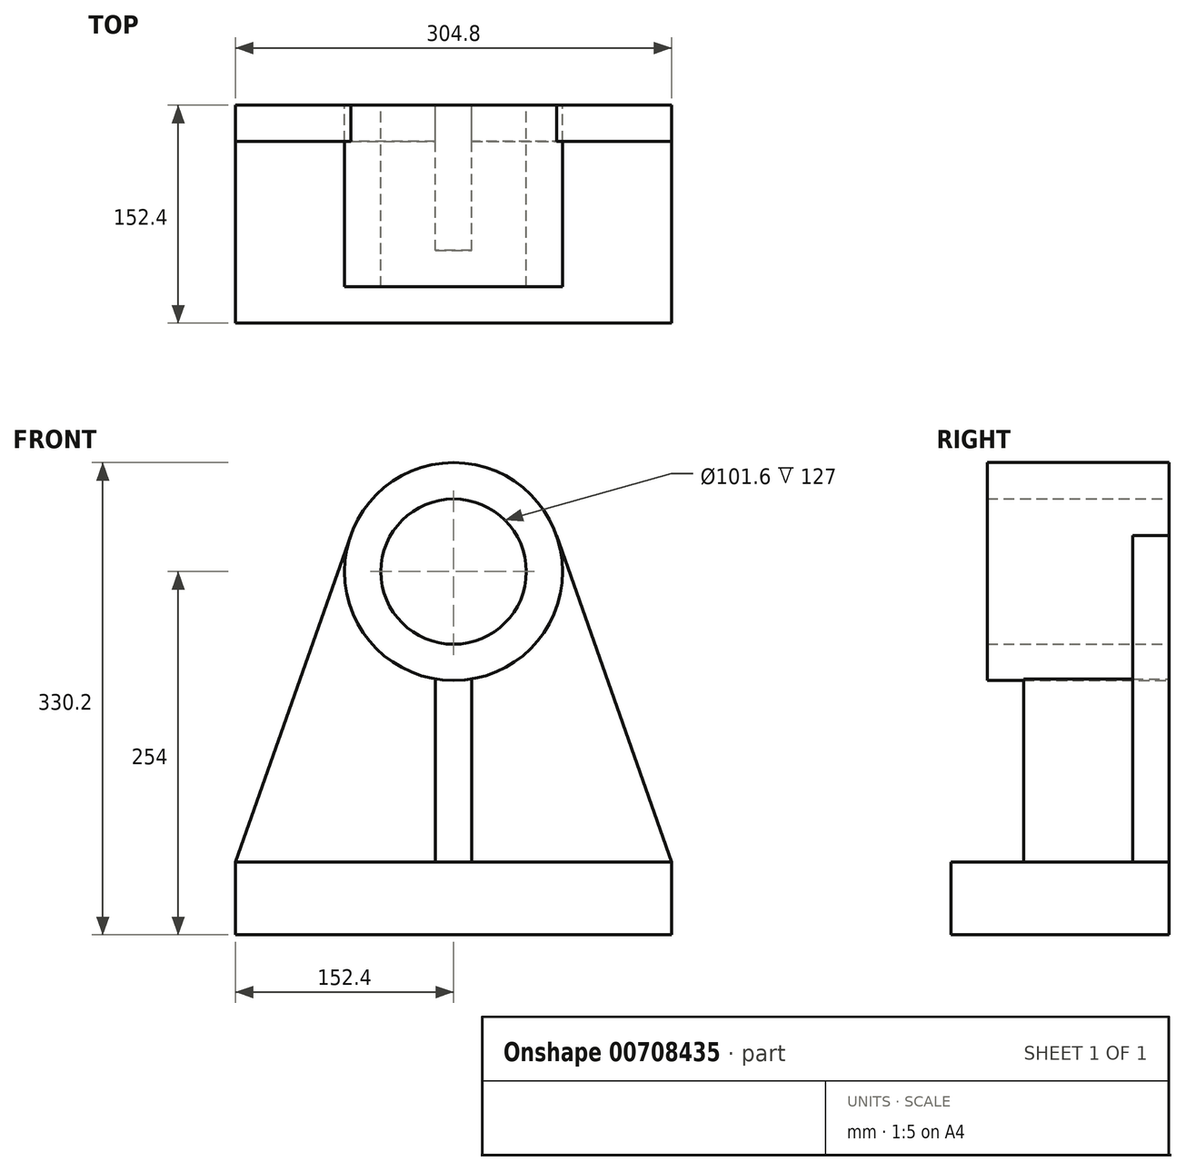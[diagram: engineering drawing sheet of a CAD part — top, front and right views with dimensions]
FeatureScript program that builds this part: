
annotation { "Feature Type Name" : "Feature", "Feature Type Description" : "" }
export const myFeature = defineFeature(function(context is Context, id is Id, definition is map)
    precondition{}
    {
        {
            var Q0;
            Q0=qCreatedBy(makeId("Front.planeOp"),FACE);
            var sketch = newSketch(context, id + "F0", { "sketchPlane" : qUnion([Q0])});
            skLineSegment(sketch, "E0.bottom", {"start": v(0, 0) * mm, "end": v(304.8, 0) * mm});
            skLineSegment(sketch, "E0.top", {"start": v(0, -50.8) * mm, "end": v(304.8, -50.8) * mm});
            skLineSegment(sketch, "E0.left", {"start": v(0, 0) * mm, "end": v(0, -50.8) * mm});
            skLineSegment(sketch, "E0.right", {"start": v(304.8, 0) * mm, "end": v(304.8, -50.8) * mm});
            skSolve(sketch);
        }
        {
            var Q0;
            Q0 = qSketchRegion(id + "F0", true);
            extrude(context, id + "F1", {"entities" : qUnion([Q0]), "oppositeDirection" : true, "depth" : 152.4 * mm, "offsetDistance" : 25.4 * mm});
        }
        {
            var Q0;
            Q0=makeQuery(id+"F1.opExtrude","CAP_FACE",FACE,{"disambiguationData":[OSD([sQuery(id+"F0.wireOp",EDGE,"E0.bottom"),sQuery(id+"F0.wireOp",EDGE,"E0.top"),sQuery(id+"F0.wireOp",EDGE,"E0.left"),sQuery(id+"F0.wireOp",EDGE,"E0.right")])],"isStart":false});
            var sketch = newSketch(context, id + "F2", { "sketchPlane" : qUnion([Q0])});
            skCircle(sketch, "E1", {"center": v(-152.4, 203.2) * mm, "radius": 76.2 * mm});
            skCircle(sketch, "E2", {"center": v(-152.4, 203.2) * mm, "radius": 50.8 * mm});
            skLineSegment(sketch, "E3", {"start": v(-139.7, 128.07) * mm, "end": v(-139.7, 0) * mm});
            skLineSegment(sketch, "E4", {"start": v(-139.7, 0) * mm, "end": v(-165.1, 0) * mm});
            skLineSegment(sketch, "E5", {"start": v(-165.1, 0) * mm, "end": v(-165.1, 128.07) * mm});
            skLineSegment(sketch, "E6", {"start": v(-224.27, 228.53) * mm, "end": v(-304.8, 0) * mm});
            skLineSegment(sketch, "E7", {"start": v(-80.53, 228.53) * mm, "end": v(0, 0) * mm});
            skSolve(sketch);
        }
        {
            var Q0;
            Q0=makeQuery(id+"F2.imprint","IMPRINT",FACE,{"disambiguationData":[TD([[makeQuery(id+"F2.imprint","IMPRINT",EDGE,{"derivedFrom":sQuery(id+"F2.wireOp",EDGE,"E2")}),-1.0]])]});
            extrude(context, id + "F3", {"entities" : qUnion([Q0]), "oppositeDirection" : true, "depth" : 127 * mm, "offsetDistance" : 25.4 * mm});
        }
        {
            var Q0;
            {var subQ0=sQuery(id+"F2.wireOp",EDGE,"E3");Q0=makeQuery(id+"F2.imprint","IMPRINT",FACE,{"disambiguationData":[TD([[makeQuery(id+"F2.imprint","IMPRINT",EDGE,{"derivedFrom":subQ0}),-1.0]])]});}
            extrude(context, id + "F4", {"entities" : qUnion([Q0]), "oppositeDirection" : true, "depth" : 101.6 * mm, "offsetDistance" : 25.4 * mm});
        }
        {
            var Q0;
            {var subQ0=sQuery(id+"F2.wireOp",EDGE,"E5");Q0=makeQuery(id+"F2.imprint","IMPRINT",FACE,{"disambiguationData":[TD([[makeQuery(id+"F2.imprint","IMPRINT",EDGE,{"derivedFrom":subQ0}),1.0]])]});}
            var Q1;
            {var subQ0=sQuery(id+"F2.wireOp",EDGE,"E3");Q1=makeQuery(id+"F2.imprint","IMPRINT",FACE,{"disambiguationData":[TD([[makeQuery(id+"F2.imprint","IMPRINT",EDGE,{"derivedFrom":subQ0}),1.0]])]});}
            extrude(context, id + "F5", {"entities" : qUnion([Q0, Q1]), "oppositeDirection" : true, "depth" : 25.4 * mm, "offsetDistance" : 25.4 * mm});
        }
    });
